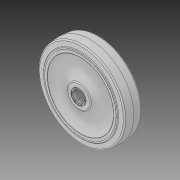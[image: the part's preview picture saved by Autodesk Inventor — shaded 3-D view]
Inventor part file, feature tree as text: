
AUTODESK INVENTOR PART (.ipt)
format: ipt  version: 2019 (Build 230136000, 136)  size: 273,408 bytes
history: native  units: in
note: dims shown in document units (in); Inventor stores cm internally (conversion verified against a paired STEP export)
features: revolve x1
ambient origin geometry x8: Origin, YZ Plane, XZ Plane, XY Plane, X Axis, Y Axis, Z Axis, Center Point
bodies: Solid1 (feature_tree)
feature tree (1):
  revolve  "Revolve1"  [1 undecoded]
note: 1 required parameter value undecoded (feature->parameter linkage not recoverable at this tier; creation-order binding heuristic only, values carry confidence <= 0.55)
